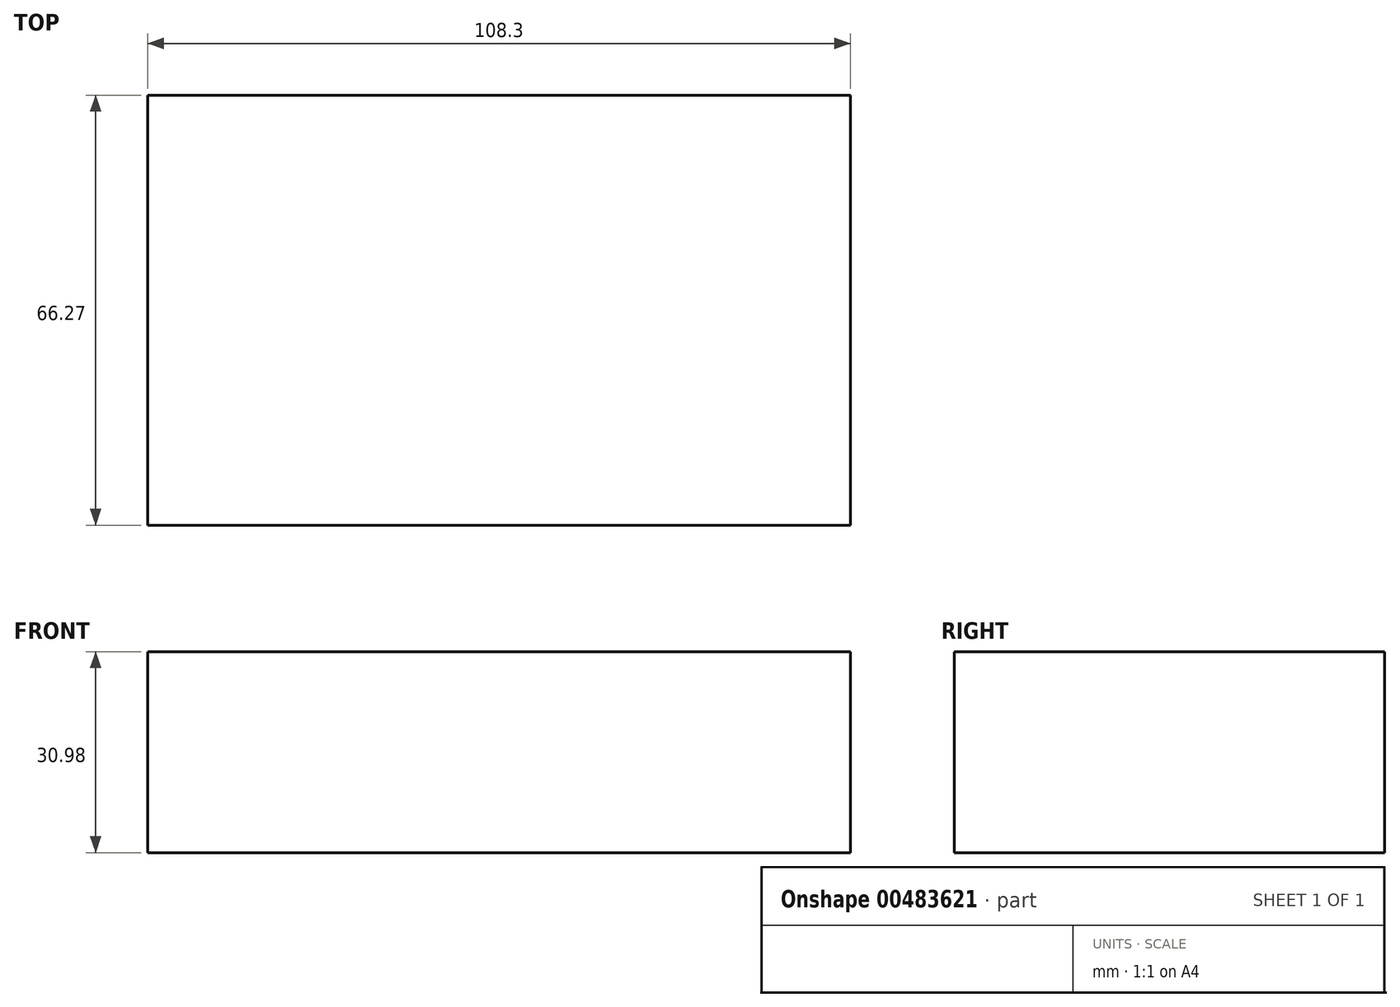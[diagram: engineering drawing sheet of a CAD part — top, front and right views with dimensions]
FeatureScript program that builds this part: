
annotation { "Feature Type Name" : "Feature", "Feature Type Description" : "" }
export const myFeature = defineFeature(function(context is Context, id is Id, definition is map)
    precondition{}
    {
        {
            var Q0;
            Q0=qCreatedBy(makeId("Front.planeOp"),FACE);
            var sketch = newSketch(context, id + "F0", { "sketchPlane" : qUnion([Q0])});
            skLineSegment(sketch, "E0.bottom", {"start": v(54.15, 15.49) * mm, "end": v(-54.15, 15.49) * mm});
            skLineSegment(sketch, "E0.top", {"start": v(54.15, -15.49) * mm, "end": v(-54.15, -15.49) * mm});
            skLineSegment(sketch, "E0.left", {"start": v(54.15, 15.49) * mm, "end": v(54.15, -15.49) * mm});
            skLineSegment(sketch, "E0.right", {"start": v(-54.15, 15.49) * mm, "end": v(-54.15, -15.49) * mm});
            skPoint(sketch, "E0.middle", {"position": v(0, 0) * mm});
            skSolve(sketch);
        }
        {
            var Q0;
            Q0 = qSketchRegion(id + "F0", true);
            extrude(context, id + "F1", {"entities" : qUnion([Q0]), "depth" : 66.27 * mm});
        }
    });
